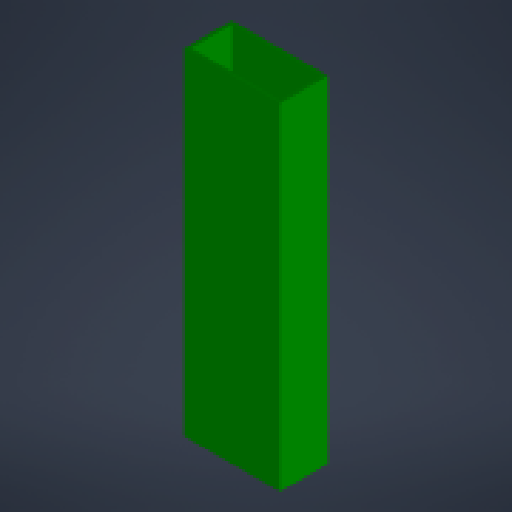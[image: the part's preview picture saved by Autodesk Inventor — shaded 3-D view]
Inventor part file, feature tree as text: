
AUTODESK INVENTOR PART (.ipt)
format: ipt  version: 2024 (Build 280153000, 153)  size: 158,720 bytes
history: native  units: mm
features: extrude x2, sketch x2
ambient origin geometry x8: Origin, YZ Plane, XZ Plane, XY Plane, X Axis, Y Axis, Z Axis, Center Point
bodies: Body1 (feature_tree)
feature tree (4):
  extrude  "Выдавливание3"  Depth=40.0mm
  extrude  "Выдавливание6"  Depth=140.0mm TaperAngle=0.0deg
  sketch  "Эскиз1"
  sketch  "Эскиз5"
